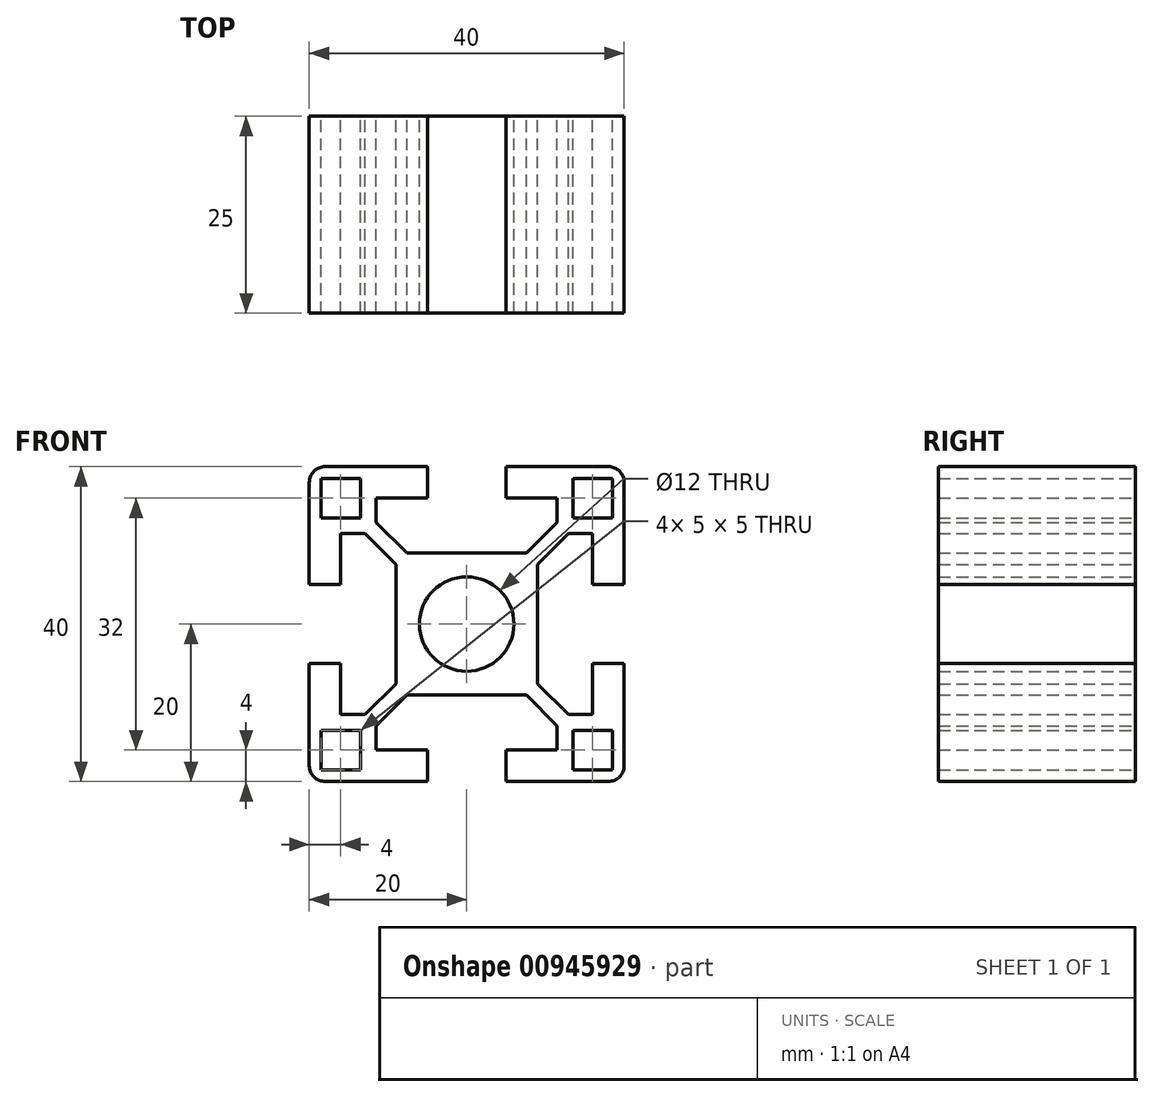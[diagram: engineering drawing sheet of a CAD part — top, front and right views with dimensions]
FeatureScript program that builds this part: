
annotation { "Feature Type Name" : "Feature", "Feature Type Description" : "" }
export const myFeature = defineFeature(function(context is Context, id is Id, definition is map)
    precondition{}
    {
        {
            var Q0;
            Q0=qCreatedBy(makeId("Front.planeOp"),FACE);
            var sketch = newSketch(context, id + "F0", { "sketchPlane" : qUnion([Q0])});
            skLineSegment(sketch, "E0.bottom", {"start": v(18, -20) * mm, "end": v(5, -20) * mm});
            skLineSegment(sketch, "E0.top", {"start": v(18, 20) * mm, "end": v(5, 20) * mm});
            skLineSegment(sketch, "E0.left", {"start": v(20, -18) * mm, "end": v(20, -5) * mm});
            skLineSegment(sketch, "E0.right", {"start": v(-20, -18) * mm, "end": v(-20, -5) * mm});
            skPoint(sketch, "E0.middle", {"position": v(0, 0) * mm});
            skLineSegment(sketch, "E1", {"start": v(0, 20) * mm, "end": v(0, -20) * mm, "construction": true});
            skLineSegment(sketch, "E2", {"start": v(-5, 20) * mm, "end": v(-5, 16) * mm});
            skLineSegment(sketch, "E3", {"start": v(-5, 16) * mm, "end": v(-11.5, 16) * mm});
            skCircle(sketch, "E4", {"center": v(0, 0) * mm, "radius": 6 * mm});
            skPoint(sketch, "E5.visualSharp", {"position": v(-20, 20) * mm});
            skArc(sketch, "E5.filletArc", {"start": v(-18, 20) * mm, "mid": v(-19.41, 19.41) * mm, "end": v(-20, 18) * mm});
            skPoint(sketch, "E6.visualSharp", {"position": v(20, 20) * mm});
            skArc(sketch, "E6.filletArc", {"start": v(20, 18) * mm, "mid": v(19.41, 19.41) * mm, "end": v(18, 20) * mm});
            skPoint(sketch, "E7.visualSharp", {"position": v(20, -20) * mm});
            skArc(sketch, "E7.filletArc", {"start": v(18, -20) * mm, "mid": v(19.41, -19.41) * mm, "end": v(20, -18) * mm});
            skPoint(sketch, "E8.visualSharp", {"position": v(-20, -20) * mm});
            skArc(sketch, "E8.filletArc", {"start": v(-20, -18) * mm, "mid": v(-19.41, -19.41) * mm, "end": v(-18, -20) * mm});
            skLineSegment(sketch, "E9", {"start": v(-7, 7) * mm, "end": v(-18, 18) * mm, "construction": true});
            skLineSegment(sketch, "E10.bottom", {"start": v(-13.5, 13.5) * mm, "end": v(-18.5, 13.5) * mm});
            skLineSegment(sketch, "E10.top", {"start": v(-13.5, 18.5) * mm, "end": v(-18.5, 18.5) * mm});
            skLineSegment(sketch, "E10.left", {"start": v(-13.5, 13.5) * mm, "end": v(-13.5, 18.5) * mm});
            skLineSegment(sketch, "E10.right", {"start": v(-18.5, 13.5) * mm, "end": v(-18.5, 18.5) * mm});
            skPoint(sketch, "E10.middle", {"position": v(-16, 16) * mm});
            skLineSegment(sketch, "E11.MirrorCS", {"start": v(5, 20) * mm, "end": v(5, 16) * mm});
            skLineSegment(sketch, "E12.MirrorCS", {"start": v(5, 16) * mm, "end": v(11.5, 16) * mm});
            skLineSegment(sketch, "E13.MirrorCS", {"start": v(13.5, 13.5) * mm, "end": v(18.5, 13.5) * mm});
            skLineSegment(sketch, "E14.MirrorCS", {"start": v(18.5, 13.5) * mm, "end": v(18.5, 18.5) * mm});
            skLineSegment(sketch, "E15.MirrorCS", {"start": v(13.5, 18.5) * mm, "end": v(18.5, 18.5) * mm});
            skLineSegment(sketch, "E16.MirrorCS", {"start": v(13.5, 13.5) * mm, "end": v(13.5, 18.5) * mm});
            skLineSegment(sketch, "E17", {"start": v(-20, 0) * mm, "end": v(20, 0) * mm, "construction": true});
            skLineSegment(sketch, "E18.trimOffspring", {"start": v(-5, 20) * mm, "end": v(-18, 20) * mm});
            skLineSegment(sketch, "E19", {"start": v(-11.5, 16) * mm, "end": v(-11.5, 12.91) * mm});
            skLineSegment(sketch, "E20", {"start": v(-11.5, 12.91) * mm, "end": v(-7.59, 9) * mm});
            skLineSegment(sketch, "E21", {"start": v(-7.59, 9) * mm, "end": v(0, 9) * mm});
            skLineSegment(sketch, "E22.MirrorCS", {"start": v(11.5, 16) * mm, "end": v(11.5, 12.91) * mm});
            skLineSegment(sketch, "E23.MirrorCS", {"start": v(11.5, 12.91) * mm, "end": v(7.59, 9) * mm});
            skLineSegment(sketch, "E24.MirrorCS", {"start": v(7.59, 9) * mm, "end": v(0, 9) * mm});
            skLineSegment(sketch, "E25.1.0", {"start": v(-20, -5) * mm, "end": v(-16, -5) * mm});
            skLineSegment(sketch, "E25.1.1", {"start": v(-16, -5) * mm, "end": v(-16, -11.5) * mm});
            skLineSegment(sketch, "E25.1.2", {"start": v(-16, -11.5) * mm, "end": v(-12.91, -11.5) * mm});
            skLineSegment(sketch, "E25.1.3", {"start": v(-12.91, -11.5) * mm, "end": v(-9, -7.59) * mm});
            skLineSegment(sketch, "E25.1.4", {"start": v(-9, -7.59) * mm, "end": v(-9, 0) * mm});
            skLineSegment(sketch, "E25.1.5", {"start": v(-9, 7.59) * mm, "end": v(-9, 0) * mm});
            skLineSegment(sketch, "E25.1.6", {"start": v(-12.91, 11.5) * mm, "end": v(-9, 7.59) * mm});
            skLineSegment(sketch, "E25.1.7", {"start": v(-16, 11.5) * mm, "end": v(-12.91, 11.5) * mm});
            skLineSegment(sketch, "E25.1.8", {"start": v(-16, 5) * mm, "end": v(-16, 11.5) * mm});
            skLineSegment(sketch, "E25.1.9", {"start": v(-20, 5) * mm, "end": v(-16, 5) * mm});
            skLineSegment(sketch, "E25.2.0", {"start": v(5, -20) * mm, "end": v(5, -16) * mm});
            skLineSegment(sketch, "E25.2.1", {"start": v(5, -16) * mm, "end": v(11.5, -16) * mm});
            skLineSegment(sketch, "E25.2.2", {"start": v(11.5, -16) * mm, "end": v(11.5, -12.91) * mm});
            skLineSegment(sketch, "E25.2.3", {"start": v(11.5, -12.91) * mm, "end": v(7.59, -9) * mm});
            skLineSegment(sketch, "E25.2.4", {"start": v(7.59, -9) * mm, "end": v(0, -9) * mm});
            skLineSegment(sketch, "E25.2.5", {"start": v(-7.59, -9) * mm, "end": v(0, -9) * mm});
            skLineSegment(sketch, "E25.2.6", {"start": v(-11.5, -12.91) * mm, "end": v(-7.59, -9) * mm});
            skLineSegment(sketch, "E25.2.7", {"start": v(-11.5, -16) * mm, "end": v(-11.5, -12.91) * mm});
            skLineSegment(sketch, "E25.2.8", {"start": v(-5, -16) * mm, "end": v(-11.5, -16) * mm});
            skLineSegment(sketch, "E25.2.9", {"start": v(-5, -20) * mm, "end": v(-5, -16) * mm});
            skLineSegment(sketch, "E26.2.3.0", {"start": v(20, 5) * mm, "end": v(16, 5) * mm});
            skLineSegment(sketch, "E26.3.3.0", {"start": v(16, 5) * mm, "end": v(16, 11.5) * mm});
            skLineSegment(sketch, "E26.6.3.0", {"start": v(16, 11.5) * mm, "end": v(12.91, 11.5) * mm});
            skLineSegment(sketch, "E26.9.3.0", {"start": v(12.91, 11.5) * mm, "end": v(9, 7.59) * mm});
            skLineSegment(sketch, "E26.12.3.0", {"start": v(9, 7.59) * mm, "end": v(9, 0) * mm});
            skLineSegment(sketch, "E26.15.3.0", {"start": v(9, -7.59) * mm, "end": v(9, 0) * mm});
            skLineSegment(sketch, "E26.18.3.0", {"start": v(12.91, -11.5) * mm, "end": v(9, -7.59) * mm});
            skLineSegment(sketch, "E26.21.3.0", {"start": v(16, -11.5) * mm, "end": v(12.91, -11.5) * mm});
            skLineSegment(sketch, "E26.24.3.0", {"start": v(16, -5) * mm, "end": v(16, -11.5) * mm});
            skLineSegment(sketch, "E26.27.3.0", {"start": v(20, -5) * mm, "end": v(16, -5) * mm});
            skLineSegment(sketch, "E27.trimOffspring", {"start": v(-20, 5) * mm, "end": v(-20, 18) * mm});
            skLineSegment(sketch, "E28.trimOffspring", {"start": v(-5, -20) * mm, "end": v(-18, -20) * mm});
            skLineSegment(sketch, "E29.trimOffspring", {"start": v(20, 5) * mm, "end": v(20, 18) * mm});
            skLineSegment(sketch, "E30.MirrorCS", {"start": v(-18.5, -13.5) * mm, "end": v(-18.5, -18.5) * mm});
            skLineSegment(sketch, "E31.MirrorCS", {"start": v(-13.5, -18.5) * mm, "end": v(-18.5, -18.5) * mm});
            skLineSegment(sketch, "E32.MirrorCS", {"start": v(-13.5, -13.5) * mm, "end": v(-13.5, -18.5) * mm});
            skLineSegment(sketch, "E33.MirrorCS", {"start": v(-13.5, -13.5) * mm, "end": v(-18.5, -13.5) * mm});
            skLineSegment(sketch, "E34.MirrorCS", {"start": v(13.5, -13.5) * mm, "end": v(13.5, -18.5) * mm});
            skLineSegment(sketch, "E35.MirrorCS", {"start": v(13.5, -18.5) * mm, "end": v(18.5, -18.5) * mm});
            skLineSegment(sketch, "E36.MirrorCS", {"start": v(18.5, -13.5) * mm, "end": v(18.5, -18.5) * mm});
            skLineSegment(sketch, "E37.MirrorCS", {"start": v(13.5, -13.5) * mm, "end": v(18.5, -13.5) * mm});
            skSolve(sketch);
        }
        {
            var Q0;
            Q0=makeQuery(id+"F0.imprint","IMPRINT",FACE,{"disambiguationData":[TD([[makeQuery(id+"F0.imprint","IMPRINT",EDGE,{"derivedFrom":sQuery(id+"F0.wireOp",EDGE,"E0.bottom")}),-1.0]])]});
            extrude(context, id + "F1", {"entities" : qUnion([Q0]), "depth" : 25 * mm, "offsetDistance" : 25 * mm});
        }
    });
